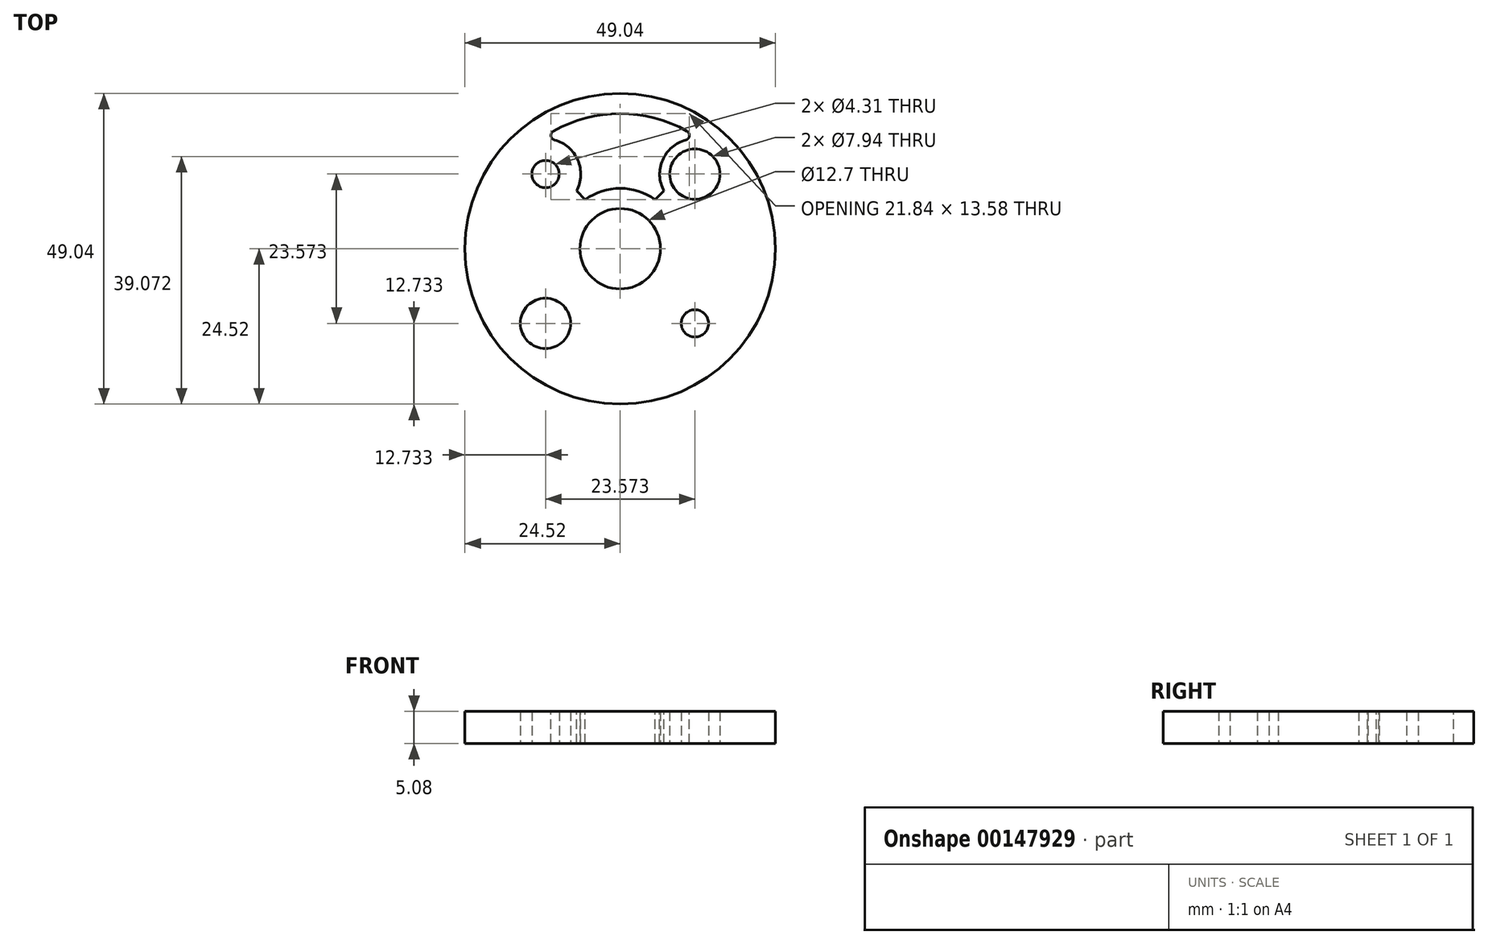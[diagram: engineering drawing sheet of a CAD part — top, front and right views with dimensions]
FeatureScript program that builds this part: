
annotation { "Feature Type Name" : "Feature", "Feature Type Description" : "" }
export const myFeature = defineFeature(function(context is Context, id is Id, definition is map)
    precondition{}
    {
        {
            var Q0;
            Q0=qCreatedBy(makeId("Top.planeOp"),FACE);
            var sketch = newSketch(context, id + "F0", { "sketchPlane" : qUnion([Q0])});
            skCircle(sketch, "E0", {"center": v(0, 0) * mm, "radius": 24.52 * mm});
            skCircle(sketch, "E1", {"center": v(0, 0) * mm, "radius": 6.35 * mm});
            skLineSegment(sketch, "E2.bottom", {"start": v(-11.79, 11.79) * mm, "end": v(11.79, 11.79) * mm, "construction": true});
            skLineSegment(sketch, "E2.top", {"start": v(-11.79, -11.79) * mm, "end": v(11.79, -11.79) * mm, "construction": true});
            skLineSegment(sketch, "E2.left", {"start": v(-11.79, 11.79) * mm, "end": v(-11.79, -11.79) * mm, "construction": true});
            skLineSegment(sketch, "E2.right", {"start": v(11.79, 11.79) * mm, "end": v(11.79, -11.79) * mm, "construction": true});
            skCircle(sketch, "E3", {"center": v(-11.79, 11.79) * mm, "radius": 7.85 * mm, "construction": true});
            skCircle(sketch, "E4", {"center": v(11.79, 11.79) * mm, "radius": 2.15 * mm, "construction": true});
            skCircle(sketch, "E5", {"center": v(-11.79, 11.79) * mm, "radius": 2.15 * mm});
            skCircle(sketch, "E6", {"center": v(-11.79, -11.79) * mm, "radius": 2.15 * mm, "construction": true});
            skCircle(sketch, "E7", {"center": v(11.79, -11.79) * mm, "radius": 2.15 * mm});
            skCircle(sketch, "E8", {"center": v(-11.79, -11.79) * mm, "radius": 3.97 * mm});
            skCircle(sketch, "E9", {"center": v(11.79, 11.79) * mm, "radius": 3.97 * mm});
            skSolve(sketch);
        }
        {
            var Q0;
            Q0=qSketchRegion(id+"F0",true);
            extrude(context, id + "F1", {"entities" : qUnion([Q0]), "depth" : 5.08 * mm});
        }
        {
            var Q0;
            Q0=makeQuery(id+"F1.opExtrude","CAP_FACE",FACE,{"disambiguationData":[OSD([sQuery(id+"F0.wireOp",EDGE,"E0"),sQuery(id+"F0.wireOp",EDGE,"E1"),sQuery(id+"F0.wireOp",EDGE,"E4"),sQuery(id+"F0.wireOp",EDGE,"E5"),sQuery(id+"F0.wireOp",EDGE,"E6"),sQuery(id+"F0.wireOp",EDGE,"E7")])],"isStart":false});
            var sketch = newSketch(context, id + "F2", { "sketchPlane" : qUnion([Q0])});
            skArc(sketch, "E10", {"start": v(-6.9, 9.14) * mm, "mid": v(-7.2, 14.93) * mm, "end": v(-12.5, 17.3) * mm});
            skArc(sketch, "E11", {"start": v(12.5, 17.3) * mm, "mid": v(7.2, 14.93) * mm, "end": v(6.9, 9.14) * mm});
            skArc(sketch, "E12", {"start": v(12.5, 17.3) * mm, "mid": v(0, 21.34) * mm, "end": v(-12.5, 17.3) * mm});
            skArc(sketch, "E13", {"start": v(5.52, 7.76) * mm, "mid": v(0, 9.53) * mm, "end": v(-5.52, 7.76) * mm});
            skLineSegment(sketch, "E14.bottom", {"start": v(-9.14, 6.9) * mm, "end": v(-6.9, 9.14) * mm, "construction": true});
            skLineSegment(sketch, "E14.top", {"start": v(-7.76, 5.52) * mm, "end": v(-5.52, 7.76) * mm, "construction": true});
            skLineSegment(sketch, "E14.left", {"start": v(-9.14, 6.9) * mm, "end": v(-7.76, 5.52) * mm, "construction": true});
            skLineSegment(sketch, "E14.right", {"start": v(-6.9, 9.14) * mm, "end": v(-5.52, 7.76) * mm});
            skLineSegment(sketch, "E15.bottom", {"start": v(9.14, 6.9) * mm, "end": v(6.9, 9.14) * mm, "construction": true});
            skLineSegment(sketch, "E15.top", {"start": v(7.76, 5.52) * mm, "end": v(5.52, 7.76) * mm, "construction": true});
            skLineSegment(sketch, "E15.left", {"start": v(9.14, 6.9) * mm, "end": v(7.76, 5.52) * mm, "construction": true});
            skLineSegment(sketch, "E15.right", {"start": v(6.9, 9.14) * mm, "end": v(5.52, 7.76) * mm});
            skLineSegment(sketch, "E16", {"start": v(-8.02, 8.02) * mm, "end": v(-11.79, 11.79) * mm, "construction": true});
            skLineSegment(sketch, "E17", {"start": v(-6.64, 6.64) * mm, "end": v(0, 0) * mm, "construction": true});
            skLineSegment(sketch, "E18", {"start": v(0, 0) * mm, "end": v(6.64, 6.64) * mm, "construction": true});
            skLineSegment(sketch, "E19", {"start": v(8.02, 8.02) * mm, "end": v(11.79, 11.79) * mm, "construction": true});
            skSolve(sketch);
        }
        {
            var Q0;
            Q0=makeQuery(id+"F2.imprint","IMPRINT",FACE,{"disambiguationData":[TD([[makeQuery(id+"F2.imprint","IMPRINT",EDGE,{"derivedFrom":sQuery(id+"F2.wireOp",EDGE,"E10")}),-1.0]])]});
            var Q1;
            Q1=makeQuery(id+"F1.opExtrude","CAP_FACE",FACE,{"disambiguationData":[OSD([sQuery(id+"F0.wireOp",EDGE,"E0"),sQuery(id+"F0.wireOp",EDGE,"E1"),sQuery(id+"F0.wireOp",EDGE,"E4"),sQuery(id+"F0.wireOp",EDGE,"E5"),sQuery(id+"F0.wireOp",EDGE,"E6"),sQuery(id+"F0.wireOp",EDGE,"E7")])],"isStart":true});
            extrude(context, id + "F3", {"entities" : qUnion([Q0]), "operationType" : NewBodyOperationType.REMOVE, "endBound" : BoundingType.UP_TO_SURFACE, "oppositeDirection" : true, "endBoundEntityFace" : qUnion([Q1]), "depth" : 25.4 * mm});
        }
        {
            var Q0;
            Q0=makeQuery(id+"F6MqURjXbY15YYN_1.1.F3.boolean.opBoolean","COPY",EDGE,{"derivedFrom":makeQuery(id+"F6MqURjXbY15YYN_1.1.F3.opExtrude","SWEPT_EDGE",EDGE,{"disambiguationData":[OSD([sQuery(id+"F2.wireOp",EDGE,"E10"),sQuery(id+"F2.wireOp",EDGE,"E12")])]})});
            var Q1;
            Q1=makeQuery(id+"F6MqURjXbY15YYN_1.1.F3.boolean.opBoolean","COPY",EDGE,{"derivedFrom":makeQuery(id+"F6MqURjXbY15YYN_1.1.F3.opExtrude","SWEPT_EDGE",EDGE,{"disambiguationData":[OSD([sQuery(id+"F2.wireOp",EDGE,"E11"),sQuery(id+"F2.wireOp",EDGE,"E12")])]})});
            var Q2;
            Q2=makeQuery(id+"F6MqURjXbY15YYN_1.2.F3.boolean.opBoolean","COPY",EDGE,{"derivedFrom":makeQuery(id+"F6MqURjXbY15YYN_1.2.F3.opExtrude","SWEPT_EDGE",EDGE,{"disambiguationData":[OSD([sQuery(id+"F2.wireOp",EDGE,"E10"),sQuery(id+"F2.wireOp",EDGE,"E12")])]})});
            var Q3;
            Q3=makeQuery(id+"F6MqURjXbY15YYN_1.2.F3.boolean.opBoolean","COPY",EDGE,{"derivedFrom":makeQuery(id+"F6MqURjXbY15YYN_1.2.F3.opExtrude","SWEPT_EDGE",EDGE,{"disambiguationData":[OSD([sQuery(id+"F2.wireOp",EDGE,"E11"),sQuery(id+"F2.wireOp",EDGE,"E12")])]})});
            var Q4;
            Q4=makeQuery(id+"F6MqURjXbY15YYN_1.3.F3.boolean.opBoolean","COPY",EDGE,{"derivedFrom":makeQuery(id+"F6MqURjXbY15YYN_1.3.F3.opExtrude","SWEPT_EDGE",EDGE,{"disambiguationData":[OSD([sQuery(id+"F2.wireOp",EDGE,"E10"),sQuery(id+"F2.wireOp",EDGE,"E12")])]})});
            var Q5;
            Q5=makeQuery(id+"F6MqURjXbY15YYN_1.3.F3.boolean.opBoolean","COPY",EDGE,{"derivedFrom":makeQuery(id+"F6MqURjXbY15YYN_1.3.F3.opExtrude","SWEPT_EDGE",EDGE,{"disambiguationData":[OSD([sQuery(id+"F2.wireOp",EDGE,"E11"),sQuery(id+"F2.wireOp",EDGE,"E12")])]})});
            var Q6;
            Q6=makeQuery(id+"F3.boolean.opBoolean","COPY",EDGE,{"derivedFrom":makeQuery(id+"F3.opExtrude","SWEPT_EDGE",EDGE,{"disambiguationData":[OSD([sQuery(id+"F2.wireOp",EDGE,"E10"),sQuery(id+"F2.wireOp",EDGE,"E12")])]})});
            var Q7;
            Q7=makeQuery(id+"F3.boolean.opBoolean","COPY",EDGE,{"derivedFrom":makeQuery(id+"F3.opExtrude","SWEPT_EDGE",EDGE,{"disambiguationData":[OSD([sQuery(id+"F2.wireOp",EDGE,"E11"),sQuery(id+"F2.wireOp",EDGE,"E12")])]})});
            fillet(context, id + "F4", {"entities" : qUnion([Q0, Q1, Q2, Q3, Q4, Q5, Q6, Q7]), "radius" : 0.76 * mm, "tangentPropagation" : true, "allowEdgeOverflow" : false});
        }
    });
